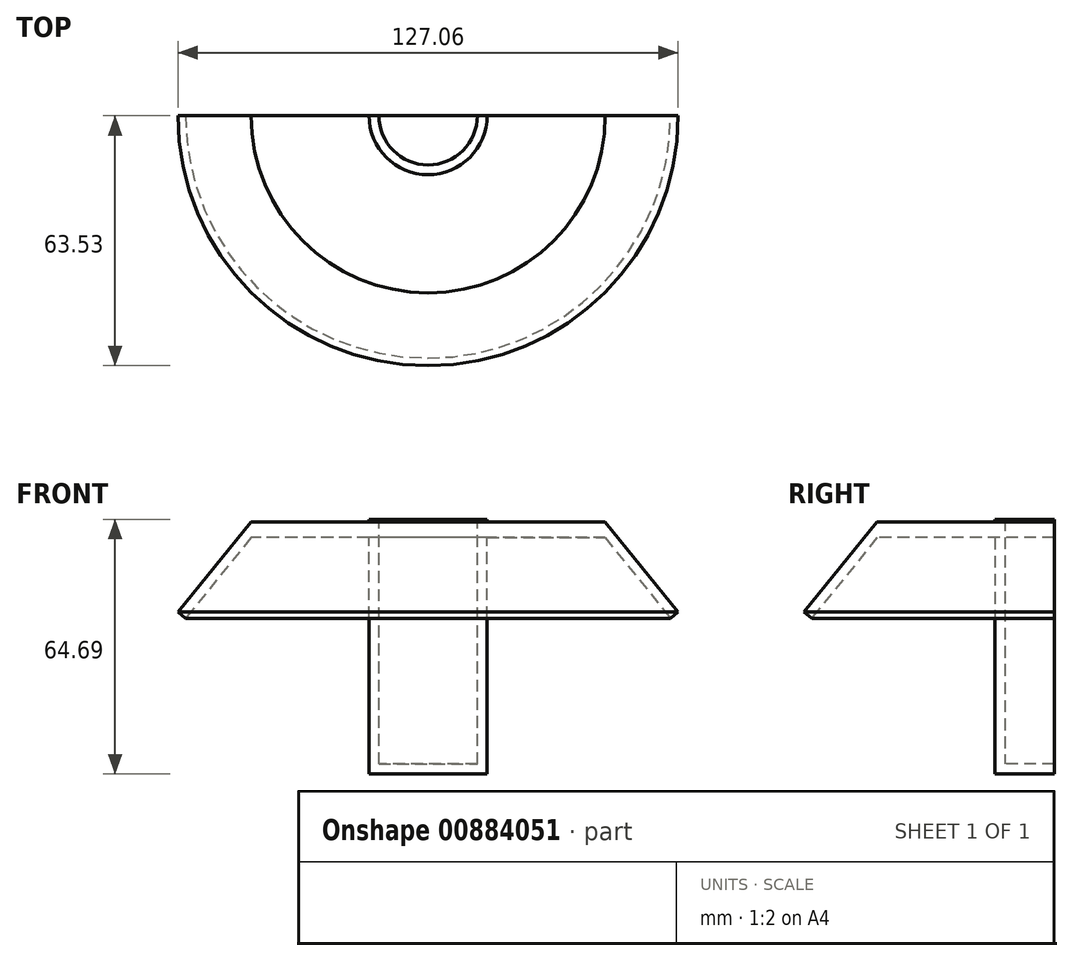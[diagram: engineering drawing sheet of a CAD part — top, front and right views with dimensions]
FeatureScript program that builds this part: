
annotation { "Feature Type Name" : "Feature", "Feature Type Description" : "" }
export const myFeature = defineFeature(function(context is Context, id is Id, definition is map)
    precondition{}
    {
        {
            var Q0;
            Q0=qCreatedBy(makeId("Right.planeOp"),FACE);
            var sketch = newSketch(context, id + "F0", { "sketchPlane" : qUnion([Q0])});
            skLineSegment(sketch, "E0", {"start": v(0, -70.82) * mm, "end": v(-15, -70.82) * mm});
            skLineSegment(sketch, "E1", {"start": v(-15, -70.82) * mm, "end": v(-15, -10.82) * mm});
            skLineSegment(sketch, "E2", {"start": v(-15, -10.82) * mm, "end": v(-45, -10.82) * mm});
            skLineSegment(sketch, "E3", {"start": v(-45, -10.82) * mm, "end": v(-61.59, -31.3) * mm});
            skLineSegment(sketch, "E4", {"start": v(-61.59, -31.3) * mm, "end": v(-63.53, -29.72) * mm});
            skLineSegment(sketch, "E5", {"start": v(-63.53, -29.72) * mm, "end": v(-45, -6.84) * mm});
            skLineSegment(sketch, "E6", {"start": v(-45, -6.84) * mm, "end": v(-15, -6.84) * mm});
            skLineSegment(sketch, "E7", {"start": v(-15, -6.84) * mm, "end": v(-15, 20.66) * mm});
            skLineSegment(sketch, "E8", {"start": v(-15, 20.66) * mm, "end": v(-12.5, 20.66) * mm});
            skPoint(sketch, "E9.start.orphan", {"position": v(0, -66.19) * mm});
            skPoint(sketch, "E10.end.orphan", {"position": v(0, -68.32) * mm});
            skLineSegment(sketch, "E11", {"start": v(0, -70.82) * mm, "end": v(0, -68.32) * mm});
            skLineSegment(sketch, "E12", {"start": v(0, -68.32) * mm, "end": v(-12.5, -68.32) * mm});
            skPoint(sketch, "E13.end.orphan", {"position": v(-12.5, -6.84) * mm});
            skLineSegment(sketch, "E14", {"start": v(-12.5, -68.32) * mm, "end": v(-12.5, 20.66) * mm});
            skSolve(sketch);
        }
        {
            var Q0;
            Q0=makeQuery(id+"F0.imprint","IMPRINT",FACE,{"disambiguationData":[TD([[makeQuery(id+"F0.imprint","IMPRINT",EDGE,{"derivedFrom":sQuery(id+"F0.wireOp",EDGE,"E0")}),-1.0]])]});
            var Q1;
            Q1=sQuery(id+"F0.wireOp",EDGE,"E11");
            revolve(context, id + "F1", {"surfaceOperationType" : NewSurfaceOperationType.NEW, "entities" : qUnion([Q0]), "axis" : qUnion([Q1]), "revolveType" : RevolveType.SYMMETRIC, "angle" : 180 * degree});
        }
        {
            var Q0;
            Q0=qCreatedBy(makeId("Front.planeOp"),FACE);
            var sketch = newSketch(context, id + "F2", { "sketchPlane" : qUnion([Q0])});
            skLineSegment(sketch, "E15", {"start": v(15.1, 20.7) * mm, "end": v(15.1, -6.13) * mm});
            skLineSegment(sketch, "E16", {"start": v(15.1, -6.13) * mm, "end": v(-15.63, -6.13) * mm});
            skLineSegment(sketch, "E17", {"start": v(-15.63, -6.13) * mm, "end": v(-15.63, 20.7) * mm});
            skLineSegment(sketch, "E18", {"start": v(-15.63, 20.7) * mm, "end": v(17.03, 20.7) * mm});
            skSolve(sketch);
        }
        {
            var Q0;
            {var subQ0=sQuery(id+"F2.wireOp",EDGE,"E15");Q0=makeQuery(id+"F2.imprint","IMPRINT",FACE,{"disambiguationData":[TD([[makeQuery(id+"F2.imprint","IMPRINT",EDGE,{"derivedFrom":subQ0}),-1.0]])]});}
            extrude(context, id + "F3", {"entities" : qUnion([Q0]), "operationType" : NewBodyOperationType.REMOVE, "depth" : 100 * mm, "offsetDistance" : 25 * mm});
        }
    });
